# Revit family: wandvefestiger
name_source: partatom
category: Generic Models
revit_build: Autodesk Revit 2017 (Build: 20160225_1515(x64)
units: mm (PartAtom-declared; Revit-internal decimal feet)

## family parameters
Always vertical = Yes
Can host rebar = No
Cut with Voids When Loaded = No
Part Type = Normal
Room Calculation Point = No
Round Connector Dimension = Use Diameter
Shared = No
Work Plane-Based = No

## types (3) — shared parameters
Manufacturer = OBO BETTERMANN
URL = http://www.obo-bettermann.com
Width = 50 mm  [stored 0.164042 ft]
zero-valued in all types: Length

## per-type parameters (varying)
| type | GTIN | Manufacturer Art.No. | Material |
| K 12 1818 FS | 4012196208876 | 6437109 | Strip-galvanised |
| K12 1818 A2 | 4012196013036 | 6016421 | Stainless steel, A2 |
| K 12 1818 FSKLGR | 4012196333370 | 6479379 | Steel |

note: column(s) folded — value = type name in every type: Article Type

note: [stored X ft] marks values corroborated as IEEE doubles in the binary element streams (Revit-internal decimal feet)

## geometry (parser evidence)
native form markers: Sweep x2
no freeform markers — native parametric forms only
